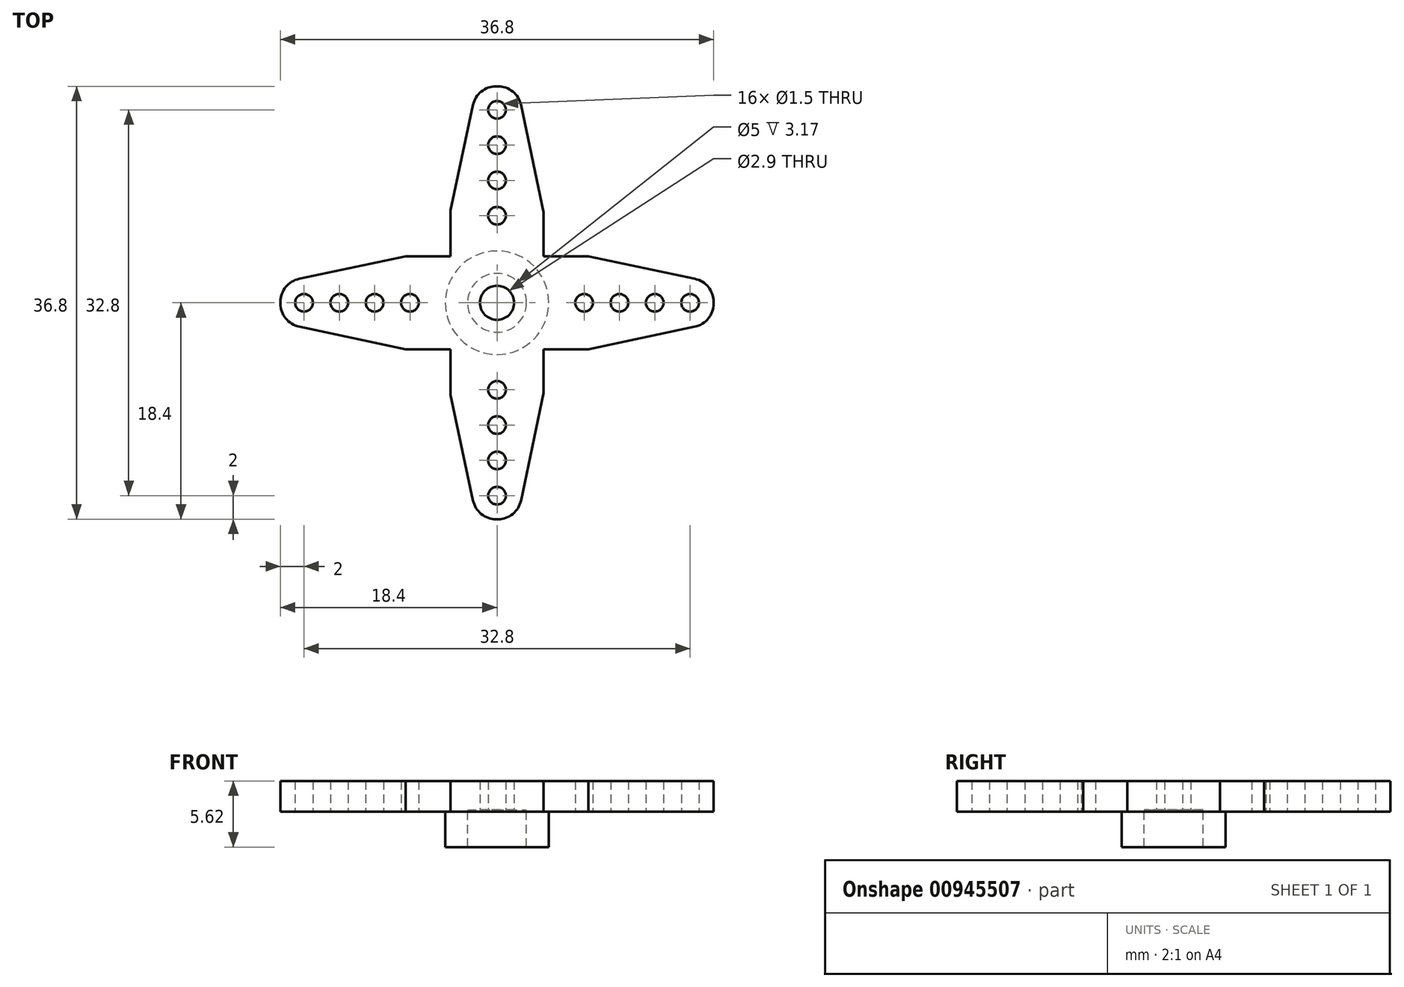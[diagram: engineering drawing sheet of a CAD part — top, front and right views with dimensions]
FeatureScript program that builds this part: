
annotation { "Feature Type Name" : "Feature", "Feature Type Description" : "" }
export const myFeature = defineFeature(function(context is Context, id is Id, definition is map)
    precondition{}
    {
        {
            var Q0;
            Q0=qCreatedBy(makeId("Top.planeOp"),FACE);
            var sketch = newSketch(context, id + "F0", { "sketchPlane" : qUnion([Q0])});
            skLineSegment(sketch, "E0.bottom", {"start": v(7.76, -3.95) * mm, "end": v(3.95, -3.95) * mm});
            skLineSegment(sketch, "E0.top", {"start": v(7.76, 3.95) * mm, "end": v(3.95, 3.95) * mm});
            skLineSegment(sketch, "E0.left", {"start": v(18.4, -0.08) * mm, "end": v(18.4, 0.08) * mm});
            skLineSegment(sketch, "E0.right", {"start": v(-18.4, -0.08) * mm, "end": v(-18.4, 0.08) * mm});
            skPoint(sketch, "E0.middle", {"position": v(0, 0) * mm});
            skLineSegment(sketch, "E1.bottom", {"start": v(0.08, 18.4) * mm, "end": v(-0.08, 18.4) * mm});
            skLineSegment(sketch, "E1.top", {"start": v(0.08, -18.4) * mm, "end": v(-0.08, -18.4) * mm});
            skLineSegment(sketch, "E1.left", {"start": v(3.95, 7.69) * mm, "end": v(3.95, 3.95) * mm});
            skLineSegment(sketch, "E1.right", {"start": v(-3.95, 7.85) * mm, "end": v(-3.95, 3.95) * mm});
            skLineSegment(sketch, "E2", {"start": v(-7.76, 3.95) * mm, "end": v(-16.81, 2.04) * mm});
            skLineSegment(sketch, "E3", {"start": v(-7.76, -3.95) * mm, "end": v(-16.81, -2.04) * mm});
            skLineSegment(sketch, "E4", {"start": v(-3.95, 7.85) * mm, "end": v(-2.04, 16.82) * mm});
            skLineSegment(sketch, "E5", {"start": v(3.95, 7.69) * mm, "end": v(2.03, 16.81) * mm});
            skPoint(sketch, "E6.newPointA", {"position": v(-18.4, 1.7) * mm});
            skArc(sketch, "E6.filletArc", {"start": v(-16.81, 2.04) * mm, "mid": v(-17.95, 1.34) * mm, "end": v(-18.4, 0.08) * mm});
            skPoint(sketch, "E7.newPointB", {"position": v(-18.4, -1.7) * mm});
            skArc(sketch, "E7.filletArc", {"start": v(-18.4, -0.08) * mm, "mid": v(-17.95, -1.34) * mm, "end": v(-16.81, -2.04) * mm});
            skPoint(sketch, "E8.orphan", {"position": v(-18.4, 3.95) * mm});
            skPoint(sketch, "E9.orphan", {"position": v(-18.4, -3.95) * mm});
            skPoint(sketch, "E10.newPointA", {"position": v(-1.7, 18.4) * mm});
            skPoint(sketch, "E10.newPointB", {"position": v(-3.95, 18.4) * mm});
            skArc(sketch, "E10.filletArc", {"start": v(-0.08, 18.4) * mm, "mid": v(-1.34, 17.95) * mm, "end": v(-2.04, 16.82) * mm});
            skPoint(sketch, "E11.newPointA", {"position": v(3.95, 18.4) * mm});
            skPoint(sketch, "E11.newPointB", {"position": v(1.7, 18.4) * mm});
            skArc(sketch, "E11.filletArc", {"start": v(2.03, 16.81) * mm, "mid": v(1.34, 17.95) * mm, "end": v(0.08, 18.4) * mm});
            skLineSegment(sketch, "E12.MirrorCS", {"start": v(7.76, 3.95) * mm, "end": v(16.81, 2.04) * mm});
            skArc(sketch, "E13.MirrorCS", {"start": v(16.81, 2.04) * mm, "mid": v(17.95, 1.34) * mm, "end": v(18.4, 0.08) * mm});
            skArc(sketch, "E14.MirrorCS", {"start": v(18.4, -0.08) * mm, "mid": v(17.95, -1.34) * mm, "end": v(16.81, -2.04) * mm});
            skLineSegment(sketch, "E15.MirrorCS", {"start": v(7.76, -3.95) * mm, "end": v(16.81, -2.04) * mm});
            skLineSegment(sketch, "E16.MirrorCS", {"start": v(-3.95, -7.85) * mm, "end": v(-2.04, -16.82) * mm});
            skArc(sketch, "E17.MirrorCS", {"start": v(-0.08, -18.4) * mm, "mid": v(-1.34, -17.95) * mm, "end": v(-2.04, -16.82) * mm});
            skArc(sketch, "E18.MirrorCS", {"start": v(2.03, -16.81) * mm, "mid": v(1.34, -17.95) * mm, "end": v(0.08, -18.4) * mm});
            skLineSegment(sketch, "E19.MirrorCS", {"start": v(3.95, -7.69) * mm, "end": v(2.03, -16.81) * mm});
            skPoint(sketch, "E20.orphan", {"position": v(18.4, 3.95) * mm});
            skPoint(sketch, "E21.orphan", {"position": v(18.4, -3.95) * mm});
            skPoint(sketch, "E22.orphan", {"position": v(3.95, -18.4) * mm});
            skPoint(sketch, "E23.orphan", {"position": v(-3.95, -18.4) * mm});
            skLineSegment(sketch, "E24.trimOffspring", {"start": v(-3.95, -3.95) * mm, "end": v(-7.76, -3.95) * mm});
            skLineSegment(sketch, "E25.trimOffspring", {"start": v(3.95, -3.95) * mm, "end": v(3.95, -7.69) * mm});
            skLineSegment(sketch, "E26.trimOffspring", {"start": v(-3.95, 3.95) * mm, "end": v(-7.76, 3.95) * mm});
            skLineSegment(sketch, "E27.trimOffspring", {"start": v(-3.95, -3.95) * mm, "end": v(-3.95, -7.85) * mm});
            skCircle(sketch, "E28", {"center": v(0, 7.4) * mm, "radius": 0.75 * mm});
            skCircle(sketch, "E29", {"center": v(0, 10.4) * mm, "radius": 0.75 * mm});
            skCircle(sketch, "E30", {"center": v(0, 13.4) * mm, "radius": 0.75 * mm});
            skCircle(sketch, "E31", {"center": v(0, 16.4) * mm, "radius": 0.75 * mm});
            skCircle(sketch, "E32", {"center": v(-16.4, 0) * mm, "radius": 0.75 * mm});
            skCircle(sketch, "E33", {"center": v(-13.4, 0) * mm, "radius": 0.75 * mm});
            skCircle(sketch, "E34", {"center": v(-10.4, 0) * mm, "radius": 0.75 * mm});
            skCircle(sketch, "E35", {"center": v(-7.4, 0) * mm, "radius": 0.75 * mm});
            skCircle(sketch, "E36.MirrorC", {"center": v(7.4, 0) * mm, "radius": 0.75 * mm});
            skCircle(sketch, "E37.MirrorC", {"center": v(10.4, 0) * mm, "radius": 0.75 * mm});
            skCircle(sketch, "E38.MirrorC", {"center": v(13.4, 0) * mm, "radius": 0.75 * mm});
            skCircle(sketch, "E39.MirrorC", {"center": v(16.4, 0) * mm, "radius": 0.75 * mm});
            skCircle(sketch, "E40.MirrorC", {"center": v(0, -7.4) * mm, "radius": 0.75 * mm});
            skCircle(sketch, "E41.MirrorC", {"center": v(0, -10.4) * mm, "radius": 0.75 * mm});
            skCircle(sketch, "E42.MirrorC", {"center": v(0, -13.4) * mm, "radius": 0.75 * mm});
            skCircle(sketch, "E43.MirrorC", {"center": v(0, -16.4) * mm, "radius": 0.75 * mm});
            skCircle(sketch, "E44", {"center": v(0, 0) * mm, "radius": 1.45 * mm});
            skSolve(sketch);
        }
        {
            var Q0;
            Q0=makeQuery(id+"F0.imprint","IMPRINT",FACE,{"disambiguationData":[TD([[makeQuery(id+"F0.imprint","IMPRINT",EDGE,{"derivedFrom":sQuery(id+"F0.wireOp",EDGE,"E0.bottom")}),-1.0]])]});
            extrude(context, id + "F1", {"entities" : qUnion([Q0]), "depth" : 2.62 * mm, "offsetDistance" : 25 * mm});
        }
        {
            var Q0;
            Q0=makeQuery(id+"F1.opExtrude","CAP_FACE",FACE,{"disambiguationData":[OSD([sQuery(id+"F0.wireOp",EDGE,"E0.bottom"),sQuery(id+"F0.wireOp",EDGE,"E0.top"),sQuery(id+"F0.wireOp",EDGE,"E0.left"),sQuery(id+"F0.wireOp",EDGE,"E0.right"),sQuery(id+"F0.wireOp",EDGE,"E1.bottom"),sQuery(id+"F0.wireOp",EDGE,"E1.top"),sQuery(id+"F0.wireOp",EDGE,"E1.left"),sQuery(id+"F0.wireOp",EDGE,"E1.right"),sQuery(id+"F0.wireOp",EDGE,"E2"),sQuery(id+"F0.wireOp",EDGE,"E3"),sQuery(id+"F0.wireOp",EDGE,"E4"),sQuery(id+"F0.wireOp",EDGE,"E5"),sQuery(id+"F0.wireOp",EDGE,"E6.filletArc"),sQuery(id+"F0.wireOp",EDGE,"E7.filletArc"),sQuery(id+"F0.wireOp",EDGE,"E10.filletArc"),sQuery(id+"F0.wireOp",EDGE,"E11.filletArc"),sQuery(id+"F0.wireOp",EDGE,"E12.MirrorCS"),sQuery(id+"F0.wireOp",EDGE,"E13.MirrorCS"),sQuery(id+"F0.wireOp",EDGE,"E14.MirrorCS"),sQuery(id+"F0.wireOp",EDGE,"E15.MirrorCS"),sQuery(id+"F0.wireOp",EDGE,"E16.MirrorCS"),sQuery(id+"F0.wireOp",EDGE,"E17.MirrorCS"),sQuery(id+"F0.wireOp",EDGE,"E18.MirrorCS"),sQuery(id+"F0.wireOp",EDGE,"E19.MirrorCS"),sQuery(id+"F0.wireOp",EDGE,"E24.trimOffspring"),sQuery(id+"F0.wireOp",EDGE,"E25.trimOffspring"),sQuery(id+"F0.wireOp",EDGE,"E26.trimOffspring"),sQuery(id+"F0.wireOp",EDGE,"E27.trimOffspring"),sQuery(id+"F0.wireOp",EDGE,"E28"),sQuery(id+"F0.wireOp",EDGE,"E29"),sQuery(id+"F0.wireOp",EDGE,"E30"),sQuery(id+"F0.wireOp",EDGE,"E31"),sQuery(id+"F0.wireOp",EDGE,"E32"),sQuery(id+"F0.wireOp",EDGE,"E33"),sQuery(id+"F0.wireOp",EDGE,"E34"),sQuery(id+"F0.wireOp",EDGE,"E35"),sQuery(id+"F0.wireOp",EDGE,"E36.MirrorC"),sQuery(id+"F0.wireOp",EDGE,"E37.MirrorC"),sQuery(id+"F0.wireOp",EDGE,"E38.MirrorC"),sQuery(id+"F0.wireOp",EDGE,"E39.MirrorC"),sQuery(id+"F0.wireOp",EDGE,"E40.MirrorC"),sQuery(id+"F0.wireOp",EDGE,"E41.MirrorC"),sQuery(id+"F0.wireOp",EDGE,"E42.MirrorC"),sQuery(id+"F0.wireOp",EDGE,"E43.MirrorC"),sQuery(id+"F0.wireOp",EDGE,"E44")])],"isStart":true});
            var sketch = newSketch(context, id + "F2", { "sketchPlane" : qUnion([Q0])});
            skCircle(sketch, "E45", {"center": v(0, 0) * mm, "radius": 4.4 * mm});
            skCircle(sketch, "E46", {"center": v(0, 0) * mm, "radius": 2.5 * mm});
            skSolve(sketch);
        }
        {
            var Q0;
            Q0=makeQuery(id+"F2.imprint","IMPRINT",FACE,{"disambiguationData":[TD([[makeQuery(id+"F2.imprint","IMPRINT",EDGE,{"derivedFrom":sQuery(id+"F2.wireOp",EDGE,"E45")}),1.0]])]});
            extrude(context, id + "F3", {"entities" : qUnion([Q0]), "operationType" : NewBodyOperationType.ADD, "depth" : 3 * mm, "offsetDistance" : 25 * mm});
        }
        {
            var Q0;
            {var subQ0=sQuery(id+"F0.wireOp",EDGE,"E44");Q0=makeQuery(id+"F3.boolean.opBoolean","SPLIT",FACE,{"disambiguationData":[TD([makeQuery(id+"F1.opExtrude","SWEPT_FACE",FACE,{"disambiguationData":[OSD([subQ0])]})])],"derivedFrom":makeQuery(id+"F1.opExtrude","CAP_FACE",FACE,{"disambiguationData":[OSD([sQuery(id+"F0.wireOp",EDGE,"E0.bottom"),sQuery(id+"F0.wireOp",EDGE,"E0.top"),sQuery(id+"F0.wireOp",EDGE,"E0.left"),sQuery(id+"F0.wireOp",EDGE,"E0.right"),sQuery(id+"F0.wireOp",EDGE,"E1.bottom"),sQuery(id+"F0.wireOp",EDGE,"E1.top"),sQuery(id+"F0.wireOp",EDGE,"E1.left"),sQuery(id+"F0.wireOp",EDGE,"E1.right"),sQuery(id+"F0.wireOp",EDGE,"E2"),sQuery(id+"F0.wireOp",EDGE,"E3"),sQuery(id+"F0.wireOp",EDGE,"E4"),sQuery(id+"F0.wireOp",EDGE,"E5"),sQuery(id+"F0.wireOp",EDGE,"E6.filletArc"),sQuery(id+"F0.wireOp",EDGE,"E7.filletArc"),sQuery(id+"F0.wireOp",EDGE,"E10.filletArc"),sQuery(id+"F0.wireOp",EDGE,"E11.filletArc"),sQuery(id+"F0.wireOp",EDGE,"E12.MirrorCS"),sQuery(id+"F0.wireOp",EDGE,"E13.MirrorCS"),sQuery(id+"F0.wireOp",EDGE,"E14.MirrorCS"),sQuery(id+"F0.wireOp",EDGE,"E15.MirrorCS"),sQuery(id+"F0.wireOp",EDGE,"E16.MirrorCS"),sQuery(id+"F0.wireOp",EDGE,"E17.MirrorCS"),sQuery(id+"F0.wireOp",EDGE,"E18.MirrorCS"),sQuery(id+"F0.wireOp",EDGE,"E19.MirrorCS"),sQuery(id+"F0.wireOp",EDGE,"E24.trimOffspring"),sQuery(id+"F0.wireOp",EDGE,"E25.trimOffspring"),sQuery(id+"F0.wireOp",EDGE,"E26.trimOffspring"),sQuery(id+"F0.wireOp",EDGE,"E27.trimOffspring"),sQuery(id+"F0.wireOp",EDGE,"E28"),sQuery(id+"F0.wireOp",EDGE,"E29"),sQuery(id+"F0.wireOp",EDGE,"E30"),sQuery(id+"F0.wireOp",EDGE,"E31"),sQuery(id+"F0.wireOp",EDGE,"E32"),sQuery(id+"F0.wireOp",EDGE,"E33"),sQuery(id+"F0.wireOp",EDGE,"E34"),sQuery(id+"F0.wireOp",EDGE,"E35"),sQuery(id+"F0.wireOp",EDGE,"E36.MirrorC"),sQuery(id+"F0.wireOp",EDGE,"E37.MirrorC"),sQuery(id+"F0.wireOp",EDGE,"E38.MirrorC"),sQuery(id+"F0.wireOp",EDGE,"E39.MirrorC"),sQuery(id+"F0.wireOp",EDGE,"E40.MirrorC"),sQuery(id+"F0.wireOp",EDGE,"E41.MirrorC"),sQuery(id+"F0.wireOp",EDGE,"E42.MirrorC"),sQuery(id+"F0.wireOp",EDGE,"E43.MirrorC"),subQ0])],"isStart":true})});}
            extrude(context, id + "F4", {"entities" : qUnion([Q0]), "operationType" : NewBodyOperationType.REMOVE, "oppositeDirection" : true, "depth" : (0.5 - 0.33) * mm, "offsetDistance" : 25 * mm});
        }
    });
